# Revit family: PRD_FrankeWS_WlHngWshBsns_QuadroWashBasin_ANMW410,411,416,417
name_source: partatom
category: Plumbing Fixtures
revit_build: Autodesk Revit 2018 (Build: 20190510_1515(x64)
units: mm (PartAtom-declared; Revit-internal decimal feet)

## family parameters
Cut with Voids When Loaded = No
Host = Face
OmniClass Number = 23.45.05.14.14
OmniClass Title = Sinks/Lavatories
Part Type = Normal
Room Calculation Point = No
Round Connector Dimension = Use Diameter
Shared = No

## types (4) — shared parameters
AssetType = Fixed
Category = Pr_40_20_96_96, Wall-hung wash basins
Color = Alpinewhite
Default Elevation = 850 mm  [stored 2.78871 ft]
DurationUnit = year
Form = Wall hung wash basin
IfcExportAs = IfcSanitaryTerminalType
IfcExportType = WASHHANDBASIN
IntegralAccessories = Mounting material included (hanger bolts and dowels)
Manufacturer = KWC Group AG
ManufacturerName = KWC Group AG
ManufacturerURL = www.kwc.com
Material = Mineral material
MaterialsBody = Miranit
MaterialsFinishAndColour = Alpinewhite
NBSDescription = Wall hung wash basins
NBSReference = 45-35-70/369
NominalDepth = 530 mm  [stored 1.73885 ft]
NominalHeight = 125 mm  [stored 0.410105 ft]
ProductInformation = https://pim.kwc.com
TypeOfMounting = Wall mounting
URL = www.kwc.com
Uniclass2015Code = Pr_40_20_96_96
Uniclass2015Title = Wall-hung wash basins
Uniclass2015Version = Products v1.10
Version = 1
WarrantyDurationUnit = year
WashHandBasinMounting = WallHung
WashbasinMaterial = PRD_AR_Miranit_Alpinewhite
WasteSize = 32  [stored 0.104987 ft]
WaterSupplyOverflowAndWasteHolesOverflow = None
WaterSupplyOverflowAndWasteHolesWaste = Center-Back

## per-type parameters (varying)
| type | BIMObjectName | Description | DrainSize | Features | GrossWeight | Model | ModelNumber | ModelReference | Name | NetWeight | NominalWidth | Size | StrainerOffset | Taphole | Type | WashHandBasinType | WaterSupplyOverflowAndWasteHolesWaterSupply |
| ANMW410 - without taphole | PRD_AR_WallHungWashBasins_QuadroWashBasin_ANMW410 | QUADRO single washbasin made of MIRANIT resin-bonded mineral material, with smooth, pore-free surface (temperature-resistant up to 80°C). With seamless, rectangular bowl without overflow. Integral back panel with integrated brackets and holes for fixing. Rear contoured edge. Three-sided apron. Mounting material included (hanger bolts and dowels). Alpine white colour. Washbasin dimensions 600 x 60 x 530 (W x H x D), bowl dimensions 520 x 40/90 x 375 (W x H x D). without taphole | DN 32 (1 1/4inch) | mineral material, wall mounting, 600x125x530 mm (WxHxD) | 19.00 kg | ANMW410 | 2000090010 | ANMW410 | QUADRO single washbasin ANMW410 | 18.05 kg | 600 mm | 530 x 125 x 600 mm | 310 mm  [stored 1.01706 ft] | No | ANMW410,411 | Other | No taphole |
| ANMW411 - with taphole | PRD_AR_WallHungWashBasins_QuadroWashBasin_ANMW411 | QUADRO single washbasin made of MIRANIT resin-bonded mineral material, with smooth, pore-free surface (temperature-resistant up to 80°C). With seamless, rectangular bowl without overflow. Integral back panel with integrated brackets and holes for fixing. Rear contoured edge. Three-sided apron. Mounting material included (hanger bolts and dowels). Alpine white colour. Washbasin dimensions 600 x 60 x 530 (W x H x D), bowl dimensions 520 x 40/90 x 375 (W x H x D). with taphole | DN 32 (1 1/4inch) | mineral material, wall mounting, 600x125x530 mm (WxHxD) | 19.00 kg | ANMW411 | 2000090011 | ANMW411 | QUADRO single washbasin ANMW411 | 18.05 kg | 600 mm | 530 x 125 x 600 mm | 310 mm  [stored 1.01706 ft] | Yes | ANMW410,411 | Other | Single tap hole, centred |
| ANMW416 - with taphole | PRD_AR_WallHungWashBasins_QuadroWashBasin_ANMW416 | QUADRO single washbasin made of MIRANIT resin-bonded mineral material, with smooth, pore-free surface (temperature-resistant up to 80°C). With seamless, rectangular bowl without overflow. Integral back panel with integrated brackets and holes for fixing. Rear contoured edge. Three-sided apron. Mounting material included (hanger bolts and dowels).
Alpine white colour. Washbasin dimensions 1000 x 60 x 530 (W x H x D), bowl dimensions 580 x 40/90 x 360 (W x H x D). With taphole | DN 32 (1 1/4inch) | mineral material, wall mounting, 1000x125x530 mm (WxHxD) | 17.00 kg | ANMW416 | 2000101159 | ANMW416 | QUADRO single washbasin ANMW416 | 17.00 kg | 1000 mm  [stored 3.28084 ft] | 530 x 125 x 1000 mm | 285 mm  [stored 0.935039 ft] | Yes | ANMW416,417 | Other | Single tap hole, centred |
| ANMW417 - without taphole | PRD_AR_WallHungWashBasins_QuadroWashBasin_ANMW417 | Single wash basin QUADRO, made of MIRANIT resin-bonded mineral material, with smooth, pore-free surface (temperature-resistant up to 80°C). Alpine white colour. With seamless, rectangular bowl, without overflow, without taphole. Integral back panel with integrated brackets and holes for fixing. Rear contoured edge. Three-sided apron. Mounting material included (hanger bolts and dowels). Washbasin dimensions 1000 x 60 x 530 (W x H x D), bowl dimensions 580 x 40/90 x 360 (W x H x D). | DN 32 (1 1/4 inch) | mineral material, wall mounting, 1000x125x530 mm (WxHxD) | 17.85 kg | ANMW417 | 2030036243 | ANMW417 | QUADRO single washbasin ANMW417 | 17.00 kg | 1000 mm  [stored 3.28084 ft] | 1000 x 530 x 125 mm | 285 mm  [stored 0.935039 ft] | No | ANMW416,417 | HandRinse | No tapholes |

note: [stored X ft] marks values corroborated as IEEE doubles in the binary element streams (Revit-internal decimal feet)

## geometry (parser evidence)
native form markers: Sweep x16
no freeform markers — native parametric forms only
